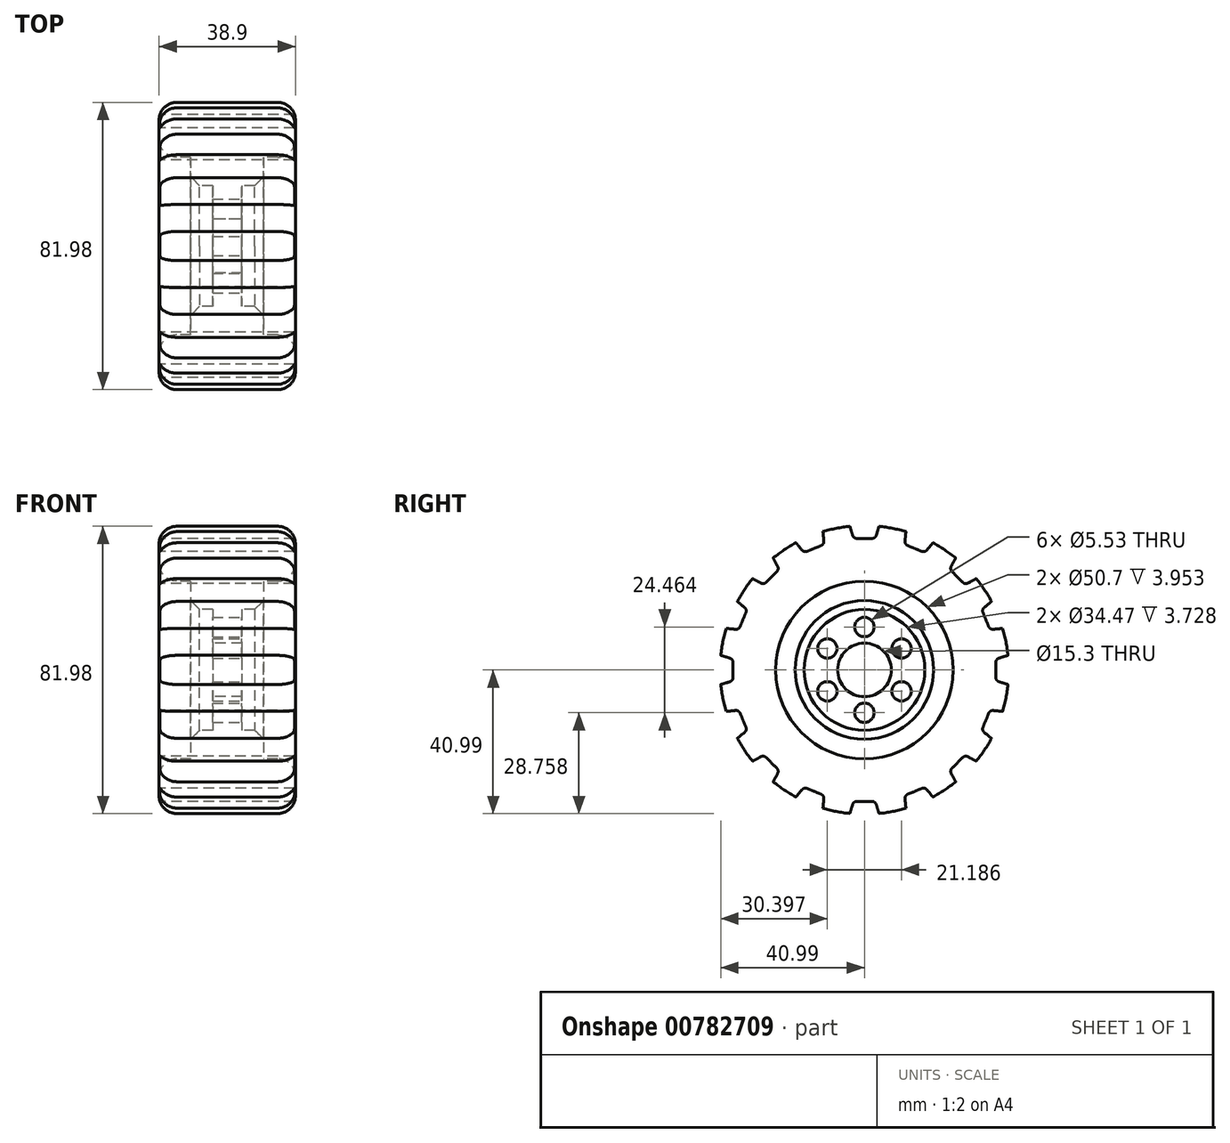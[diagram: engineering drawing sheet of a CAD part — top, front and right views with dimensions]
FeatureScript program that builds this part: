
annotation { "Feature Type Name" : "Feature", "Feature Type Description" : "" }
export const myFeature = defineFeature(function(context is Context, id is Id, definition is map)
    precondition{}
    {
        {
            var Q0;
            Q0=qCreatedBy(makeId("Front.planeOp"),FACE);
            var sketch = newSketch(context, id + "F0", { "sketchPlane" : qUnion([Q0])});
            skLineSegment(sketch, "E0", {"start": v(0, 41.2) * mm, "end": v(-19.45, 41.2) * mm});
            skLineSegment(sketch, "E1", {"start": v(-19.45, 41.2) * mm, "end": v(-19.45, 25.35) * mm});
            skLineSegment(sketch, "E2", {"start": v(-19.45, 25.35) * mm, "end": v(-10.42, 25.35) * mm});
            skLineSegment(sketch, "E3", {"start": v(-10.42, 25.35) * mm, "end": v(-10.42, 17.24) * mm});
            skLineSegment(sketch, "E4", {"start": v(-10.42, 17.24) * mm, "end": v(-4.15, 17.24) * mm});
            skLineSegment(sketch, "E5", {"start": v(-4.15, 17.24) * mm, "end": v(-4.15, 7.65) * mm});
            skLineSegment(sketch, "E6", {"start": v(-4.15, 7.65) * mm, "end": v(0, 7.65) * mm});
            skLineSegment(sketch, "E7.MirrorCS", {"start": v(0, 41.2) * mm, "end": v(19.45, 41.2) * mm});
            skLineSegment(sketch, "E8.MirrorCS", {"start": v(19.45, 41.2) * mm, "end": v(19.45, 25.35) * mm});
            skLineSegment(sketch, "E9.MirrorCS", {"start": v(19.45, 25.35) * mm, "end": v(10.42, 25.35) * mm});
            skLineSegment(sketch, "E10.MirrorCS", {"start": v(10.42, 25.35) * mm, "end": v(10.42, 17.24) * mm});
            skLineSegment(sketch, "E11.MirrorCS", {"start": v(10.42, 17.24) * mm, "end": v(4.15, 17.24) * mm});
            skLineSegment(sketch, "E12.MirrorCS", {"start": v(4.15, 7.65) * mm, "end": v(0, 7.65) * mm});
            skLineSegment(sketch, "E13.MirrorCS", {"start": v(4.15, 17.24) * mm, "end": v(4.15, 7.65) * mm});
            skLineSegment(sketch, "E14", {"start": v(-19.63, 0) * mm, "end": v(22.95, 0) * mm});
            skSolve(sketch);
        }
        {
            var Q0;
            Q0=makeQuery(id+"F0.imprint","IMPRINT",FACE,{"disambiguationData":[TD([[makeQuery(id+"F0.imprint","IMPRINT",EDGE,{"derivedFrom":sQuery(id+"F0.wireOp",EDGE,"E0")}),1.0]])]});
            var Q1;
            Q1=sQuery(id+"F0.wireOp",EDGE,"E14");
            revolve(context, id + "F1", {"surfaceOperationType" : NewSurfaceOperationType.NEW, "entities" : qUnion([Q0]), "axis" : qUnion([Q1]), "revolveType" : RevolveType.FULL});
        }
        {
            var Q0;
            Q0=makeQuery(id+"F1.opRevolve","SWEPT_EDGE",EDGE,{"disambiguationData":[OSD([sQuery(id+"F0.wireOp",EDGE,"E0"),sQuery(id+"F0.wireOp",EDGE,"E1")])]});
            var Q1;
            Q1=makeQuery(id+"F1.opRevolve","SWEPT_EDGE",EDGE,{"disambiguationData":[OSD([sQuery(id+"F0.wireOp",EDGE,"E1"),sQuery(id+"F0.wireOp",EDGE,"E2")])]});
            fillet(context, id + "F2", {"entities" : qUnion([Q0, Q1]), "radius" : 5.08 * mm, "tangentPropagation" : true, "allowEdgeOverflow" : false});
        }
        {
            var Q0;
            Q0=makeQuery(id+"F1.opRevolve","SWEPT_EDGE",EDGE,{"disambiguationData":[OSD([sQuery(id+"F0.wireOp",EDGE,"E7.MirrorCS"),sQuery(id+"F0.wireOp",EDGE,"E8.MirrorCS")])]});
            var Q1;
            Q1=makeQuery(id+"F1.opRevolve","SWEPT_EDGE",EDGE,{"disambiguationData":[OSD([sQuery(id+"F0.wireOp",EDGE,"E8.MirrorCS"),sQuery(id+"F0.wireOp",EDGE,"E9.MirrorCS")])]});
            fillet(context, id + "F3", {"entities" : qUnion([Q0, Q1]), "radius" : 5.08 * mm, "tangentPropagation" : true, "allowEdgeOverflow" : false});
        }
        {
            var Q0;
            Q0=makeQuery(id+"F1.opRevolve","SWEPT_EDGE",EDGE,{"disambiguationData":[OSD([sQuery(id+"F0.wireOp",EDGE,"E3"),sQuery(id+"F0.wireOp",EDGE,"E4")])]});
            chamfer(context, id + "F4", {"entities" : qUnion([Q0]), "width" : 2.54 * mm, "tangentPropagation" : true});
        }
        {
            var Q0;
            Q0=makeQuery(id+"F1.opRevolve","SWEPT_EDGE",EDGE,{"disambiguationData":[OSD([sQuery(id+"F0.wireOp",EDGE,"E10.MirrorCS"),sQuery(id+"F0.wireOp",EDGE,"E11.MirrorCS")])]});
            chamfer(context, id + "F5", {"entities" : qUnion([Q0]), "width" : 2.54 * mm, "tangentPropagation" : true});
        }
        {
            var Q0;
            Q0=qCreatedBy(makeId("Right.planeOp"),FACE);
            var sketch = newSketch(context, id + "F6", { "sketchPlane" : qUnion([Q0])});
            skLineSegment(sketch, "E15", {"start": v(4.44, 41.92) * mm, "end": v(3.38, 38.42) * mm});
            skLineSegment(sketch, "E16", {"start": v(2.16, 37.52) * mm, "end": v(0, 37.52) * mm});
            skLineSegment(sketch, "E17.MirrorCS", {"start": v(-4.44, 41.92) * mm, "end": v(-3.38, 38.42) * mm});
            skLineSegment(sketch, "E18.MirrorCS", {"start": v(-2.16, 37.52) * mm, "end": v(0, 37.52) * mm});
            skLineSegment(sketch, "E19", {"start": v(4.44, 41.92) * mm, "end": v(-4.44, 41.92) * mm});
            skPoint(sketch, "E20.visualSharp", {"position": v(3.1, 37.52) * mm});
            skArc(sketch, "E20.filletArc", {"start": v(2.16, 37.52) * mm, "mid": v(2.92, 37.77) * mm, "end": v(3.38, 38.42) * mm});
            skPoint(sketch, "E21.visualSharp", {"position": v(-3.1, 37.52) * mm});
            skArc(sketch, "E21.filletArc", {"start": v(-3.38, 38.42) * mm, "mid": v(-2.92, 37.77) * mm, "end": v(-2.16, 37.52) * mm});
            skLineSegment(sketch, "E22.1.0", {"start": v(-11.94, 40.43) * mm, "end": v(-20.14, 37.03) * mm});
            skLineSegment(sketch, "E22.1.1", {"start": v(-11.94, 40.43) * mm, "end": v(-11.58, 36.79) * mm});
            skArc(sketch, "E22.1.2", {"start": v(-12.36, 35.5) * mm, "mid": v(-11.76, 36.01) * mm, "end": v(-11.58, 36.79) * mm});
            skLineSegment(sketch, "E22.1.3", {"start": v(-12.36, 35.5) * mm, "end": v(-14.36, 34.66) * mm});
            skLineSegment(sketch, "E22.1.4", {"start": v(-16.36, 33.84) * mm, "end": v(-14.36, 34.66) * mm});
            skArc(sketch, "E22.1.5", {"start": v(-17.82, 34.2) * mm, "mid": v(-17.15, 33.78) * mm, "end": v(-16.36, 33.84) * mm});
            skLineSegment(sketch, "E22.1.6", {"start": v(-20.14, 37.03) * mm, "end": v(-17.82, 34.2) * mm});
            skLineSegment(sketch, "E22.2.0", {"start": v(-26.5, 32.78) * mm, "end": v(-32.78, 26.5) * mm});
            skLineSegment(sketch, "E22.2.1", {"start": v(-26.5, 32.78) * mm, "end": v(-24.78, 29.56) * mm});
            skArc(sketch, "E22.2.2", {"start": v(-25, 28.06) * mm, "mid": v(-24.64, 28.77) * mm, "end": v(-24.78, 29.56) * mm});
            skLineSegment(sketch, "E22.2.3", {"start": v(-25, 28.06) * mm, "end": v(-26.53, 26.53) * mm});
            skLineSegment(sketch, "E22.2.4", {"start": v(-28.06, 25) * mm, "end": v(-26.53, 26.53) * mm});
            skArc(sketch, "E22.2.5", {"start": v(-29.56, 24.78) * mm, "mid": v(-28.77, 24.64) * mm, "end": v(-28.06, 25) * mm});
            skLineSegment(sketch, "E22.2.6", {"start": v(-32.78, 26.5) * mm, "end": v(-29.56, 24.78) * mm});
            skLineSegment(sketch, "E22.3.0", {"start": v(-37.03, 20.14) * mm, "end": v(-40.43, 11.94) * mm});
            skLineSegment(sketch, "E22.3.1", {"start": v(-37.03, 20.14) * mm, "end": v(-34.2, 17.82) * mm});
            skArc(sketch, "E22.3.2", {"start": v(-33.84, 16.36) * mm, "mid": v(-33.78, 17.15) * mm, "end": v(-34.2, 17.82) * mm});
            skLineSegment(sketch, "E22.3.3", {"start": v(-33.84, 16.36) * mm, "end": v(-34.66, 14.36) * mm});
            skLineSegment(sketch, "E22.3.4", {"start": v(-35.5, 12.36) * mm, "end": v(-34.66, 14.36) * mm});
            skArc(sketch, "E22.3.5", {"start": v(-36.79, 11.58) * mm, "mid": v(-36.01, 11.76) * mm, "end": v(-35.5, 12.36) * mm});
            skLineSegment(sketch, "E22.3.6", {"start": v(-40.43, 11.94) * mm, "end": v(-36.79, 11.58) * mm});
            skLineSegment(sketch, "E22.4.0", {"start": v(-41.92, 4.44) * mm, "end": v(-41.92, -4.44) * mm});
            skLineSegment(sketch, "E22.4.1", {"start": v(-41.92, 4.44) * mm, "end": v(-38.42, 3.38) * mm});
            skArc(sketch, "E22.4.2", {"start": v(-37.52, 2.16) * mm, "mid": v(-37.77, 2.92) * mm, "end": v(-38.42, 3.38) * mm});
            skLineSegment(sketch, "E22.4.3", {"start": v(-37.52, 2.16) * mm, "end": v(-37.52, 0) * mm});
            skLineSegment(sketch, "E22.4.4", {"start": v(-37.52, -2.16) * mm, "end": v(-37.52, 0) * mm});
            skArc(sketch, "E22.4.5", {"start": v(-38.42, -3.38) * mm, "mid": v(-37.77, -2.92) * mm, "end": v(-37.52, -2.16) * mm});
            skLineSegment(sketch, "E22.4.6", {"start": v(-41.92, -4.44) * mm, "end": v(-38.42, -3.38) * mm});
            skLineSegment(sketch, "E22.5.0", {"start": v(-40.43, -11.94) * mm, "end": v(-37.03, -20.14) * mm});
            skLineSegment(sketch, "E22.5.1", {"start": v(-40.43, -11.94) * mm, "end": v(-36.79, -11.58) * mm});
            skArc(sketch, "E22.5.2", {"start": v(-35.5, -12.36) * mm, "mid": v(-36.01, -11.76) * mm, "end": v(-36.79, -11.58) * mm});
            skLineSegment(sketch, "E22.5.3", {"start": v(-35.5, -12.36) * mm, "end": v(-34.66, -14.36) * mm});
            skLineSegment(sketch, "E22.5.4", {"start": v(-33.84, -16.36) * mm, "end": v(-34.66, -14.36) * mm});
            skArc(sketch, "E22.5.5", {"start": v(-34.2, -17.82) * mm, "mid": v(-33.78, -17.15) * mm, "end": v(-33.84, -16.36) * mm});
            skLineSegment(sketch, "E22.5.6", {"start": v(-37.03, -20.14) * mm, "end": v(-34.2, -17.82) * mm});
            skLineSegment(sketch, "E22.6.0", {"start": v(-32.78, -26.5) * mm, "end": v(-26.5, -32.78) * mm});
            skLineSegment(sketch, "E22.6.1", {"start": v(-32.78, -26.5) * mm, "end": v(-29.56, -24.78) * mm});
            skArc(sketch, "E22.6.2", {"start": v(-28.06, -25) * mm, "mid": v(-28.77, -24.64) * mm, "end": v(-29.56, -24.78) * mm});
            skLineSegment(sketch, "E22.6.3", {"start": v(-28.06, -25) * mm, "end": v(-26.53, -26.53) * mm});
            skLineSegment(sketch, "E22.6.4", {"start": v(-25, -28.06) * mm, "end": v(-26.53, -26.53) * mm});
            skArc(sketch, "E22.6.5", {"start": v(-24.78, -29.56) * mm, "mid": v(-24.64, -28.77) * mm, "end": v(-25, -28.06) * mm});
            skLineSegment(sketch, "E22.6.6", {"start": v(-26.5, -32.78) * mm, "end": v(-24.78, -29.56) * mm});
            skLineSegment(sketch, "E22.7.0", {"start": v(-20.14, -37.03) * mm, "end": v(-11.94, -40.43) * mm});
            skLineSegment(sketch, "E22.7.1", {"start": v(-20.14, -37.03) * mm, "end": v(-17.82, -34.2) * mm});
            skArc(sketch, "E22.7.2", {"start": v(-16.36, -33.84) * mm, "mid": v(-17.15, -33.78) * mm, "end": v(-17.82, -34.2) * mm});
            skLineSegment(sketch, "E22.7.3", {"start": v(-16.36, -33.84) * mm, "end": v(-14.36, -34.66) * mm});
            skLineSegment(sketch, "E22.7.4", {"start": v(-12.36, -35.5) * mm, "end": v(-14.36, -34.66) * mm});
            skArc(sketch, "E22.7.5", {"start": v(-11.58, -36.79) * mm, "mid": v(-11.76, -36.01) * mm, "end": v(-12.36, -35.5) * mm});
            skLineSegment(sketch, "E22.7.6", {"start": v(-11.94, -40.43) * mm, "end": v(-11.58, -36.79) * mm});
            skLineSegment(sketch, "E22.8.0", {"start": v(-4.44, -41.92) * mm, "end": v(4.44, -41.92) * mm});
            skLineSegment(sketch, "E22.8.1", {"start": v(-4.44, -41.92) * mm, "end": v(-3.38, -38.42) * mm});
            skArc(sketch, "E22.8.2", {"start": v(-2.16, -37.52) * mm, "mid": v(-2.92, -37.77) * mm, "end": v(-3.38, -38.42) * mm});
            skLineSegment(sketch, "E22.8.3", {"start": v(-2.16, -37.52) * mm, "end": v(0, -37.52) * mm});
            skLineSegment(sketch, "E22.8.4", {"start": v(2.16, -37.52) * mm, "end": v(0, -37.52) * mm});
            skArc(sketch, "E22.8.5", {"start": v(3.38, -38.42) * mm, "mid": v(2.92, -37.77) * mm, "end": v(2.16, -37.52) * mm});
            skLineSegment(sketch, "E22.8.6", {"start": v(4.44, -41.92) * mm, "end": v(3.38, -38.42) * mm});
            skLineSegment(sketch, "E22.9.0", {"start": v(11.94, -40.43) * mm, "end": v(20.14, -37.03) * mm});
            skLineSegment(sketch, "E22.9.1", {"start": v(11.94, -40.43) * mm, "end": v(11.58, -36.79) * mm});
            skArc(sketch, "E22.9.2", {"start": v(12.36, -35.5) * mm, "mid": v(11.76, -36.01) * mm, "end": v(11.58, -36.79) * mm});
            skLineSegment(sketch, "E22.9.3", {"start": v(12.36, -35.5) * mm, "end": v(14.36, -34.66) * mm});
            skLineSegment(sketch, "E22.9.4", {"start": v(16.36, -33.84) * mm, "end": v(14.36, -34.66) * mm});
            skArc(sketch, "E22.9.5", {"start": v(17.82, -34.2) * mm, "mid": v(17.15, -33.78) * mm, "end": v(16.36, -33.84) * mm});
            skLineSegment(sketch, "E22.9.6", {"start": v(20.14, -37.03) * mm, "end": v(17.82, -34.2) * mm});
            skLineSegment(sketch, "E22.10.0", {"start": v(26.5, -32.78) * mm, "end": v(32.78, -26.5) * mm});
            skLineSegment(sketch, "E22.10.1", {"start": v(26.5, -32.78) * mm, "end": v(24.78, -29.56) * mm});
            skArc(sketch, "E22.10.2", {"start": v(25, -28.06) * mm, "mid": v(24.64, -28.77) * mm, "end": v(24.78, -29.56) * mm});
            skLineSegment(sketch, "E22.10.3", {"start": v(25, -28.06) * mm, "end": v(26.53, -26.53) * mm});
            skLineSegment(sketch, "E22.10.4", {"start": v(28.06, -25) * mm, "end": v(26.53, -26.53) * mm});
            skArc(sketch, "E22.10.5", {"start": v(29.56, -24.78) * mm, "mid": v(28.77, -24.64) * mm, "end": v(28.06, -25) * mm});
            skLineSegment(sketch, "E22.10.6", {"start": v(32.78, -26.5) * mm, "end": v(29.56, -24.78) * mm});
            skLineSegment(sketch, "E22.11.0", {"start": v(37.03, -20.14) * mm, "end": v(40.43, -11.94) * mm});
            skLineSegment(sketch, "E22.11.1", {"start": v(37.03, -20.14) * mm, "end": v(34.2, -17.82) * mm});
            skArc(sketch, "E22.11.2", {"start": v(33.84, -16.36) * mm, "mid": v(33.78, -17.15) * mm, "end": v(34.2, -17.82) * mm});
            skLineSegment(sketch, "E22.11.3", {"start": v(33.84, -16.36) * mm, "end": v(34.66, -14.36) * mm});
            skLineSegment(sketch, "E22.11.4", {"start": v(35.5, -12.36) * mm, "end": v(34.66, -14.36) * mm});
            skArc(sketch, "E22.11.5", {"start": v(36.79, -11.58) * mm, "mid": v(36.01, -11.76) * mm, "end": v(35.5, -12.36) * mm});
            skLineSegment(sketch, "E22.11.6", {"start": v(40.43, -11.94) * mm, "end": v(36.79, -11.58) * mm});
            skLineSegment(sketch, "E22.12.0", {"start": v(41.92, -4.44) * mm, "end": v(41.92, 4.44) * mm});
            skLineSegment(sketch, "E22.12.1", {"start": v(41.92, -4.44) * mm, "end": v(38.42, -3.38) * mm});
            skArc(sketch, "E22.12.2", {"start": v(37.52, -2.16) * mm, "mid": v(37.77, -2.92) * mm, "end": v(38.42, -3.38) * mm});
            skLineSegment(sketch, "E22.12.3", {"start": v(37.52, -2.16) * mm, "end": v(37.52, 0) * mm});
            skLineSegment(sketch, "E22.12.4", {"start": v(37.52, 2.16) * mm, "end": v(37.52, 0) * mm});
            skArc(sketch, "E22.12.5", {"start": v(38.42, 3.38) * mm, "mid": v(37.77, 2.92) * mm, "end": v(37.52, 2.16) * mm});
            skLineSegment(sketch, "E22.12.6", {"start": v(41.92, 4.44) * mm, "end": v(38.42, 3.38) * mm});
            skLineSegment(sketch, "E22.13.0", {"start": v(40.43, 11.94) * mm, "end": v(37.03, 20.14) * mm});
            skLineSegment(sketch, "E22.13.1", {"start": v(40.43, 11.94) * mm, "end": v(36.79, 11.58) * mm});
            skArc(sketch, "E22.13.2", {"start": v(35.5, 12.36) * mm, "mid": v(36.01, 11.76) * mm, "end": v(36.79, 11.58) * mm});
            skLineSegment(sketch, "E22.13.3", {"start": v(35.5, 12.36) * mm, "end": v(34.66, 14.36) * mm});
            skLineSegment(sketch, "E22.13.4", {"start": v(33.84, 16.36) * mm, "end": v(34.66, 14.36) * mm});
            skArc(sketch, "E22.13.5", {"start": v(34.2, 17.82) * mm, "mid": v(33.78, 17.15) * mm, "end": v(33.84, 16.36) * mm});
            skLineSegment(sketch, "E22.13.6", {"start": v(37.03, 20.14) * mm, "end": v(34.2, 17.82) * mm});
            skLineSegment(sketch, "E22.14.0", {"start": v(32.78, 26.5) * mm, "end": v(26.5, 32.78) * mm});
            skLineSegment(sketch, "E22.14.1", {"start": v(32.78, 26.5) * mm, "end": v(29.56, 24.78) * mm});
            skArc(sketch, "E22.14.2", {"start": v(28.06, 25) * mm, "mid": v(28.77, 24.64) * mm, "end": v(29.56, 24.78) * mm});
            skLineSegment(sketch, "E22.14.3", {"start": v(28.06, 25) * mm, "end": v(26.53, 26.53) * mm});
            skLineSegment(sketch, "E22.14.4", {"start": v(25, 28.06) * mm, "end": v(26.53, 26.53) * mm});
            skArc(sketch, "E22.14.5", {"start": v(24.78, 29.56) * mm, "mid": v(24.64, 28.77) * mm, "end": v(25, 28.06) * mm});
            skLineSegment(sketch, "E22.14.6", {"start": v(26.5, 32.78) * mm, "end": v(24.78, 29.56) * mm});
            skLineSegment(sketch, "E22.15.0", {"start": v(20.14, 37.03) * mm, "end": v(11.94, 40.43) * mm});
            skLineSegment(sketch, "E22.15.1", {"start": v(20.14, 37.03) * mm, "end": v(17.82, 34.2) * mm});
            skArc(sketch, "E22.15.2", {"start": v(16.36, 33.84) * mm, "mid": v(17.15, 33.78) * mm, "end": v(17.82, 34.2) * mm});
            skLineSegment(sketch, "E22.15.3", {"start": v(16.36, 33.84) * mm, "end": v(14.36, 34.66) * mm});
            skLineSegment(sketch, "E22.15.4", {"start": v(12.36, 35.5) * mm, "end": v(14.36, 34.66) * mm});
            skArc(sketch, "E22.15.5", {"start": v(11.58, 36.79) * mm, "mid": v(11.76, 36.01) * mm, "end": v(12.36, 35.5) * mm});
            skLineSegment(sketch, "E22.15.6", {"start": v(11.94, 40.43) * mm, "end": v(11.58, 36.79) * mm});
            skPoint(sketch, "E22.center", {"position": v(0, 0) * mm});
            skSolve(sketch);
        }
        {
            var Q0;
            Q0=makeQuery(id+"F6.imprint","IMPRINT",FACE,{"disambiguationData":[TD([[makeQuery(id+"F6.imprint","IMPRINT",EDGE,{"derivedFrom":sQuery(id+"F6.wireOp",EDGE,"E22.14.0")}),1.0]])]});
            var Q1;
            Q1=makeQuery(id+"F6.imprint","IMPRINT",FACE,{"disambiguationData":[TD([[makeQuery(id+"F6.imprint","IMPRINT",EDGE,{"derivedFrom":sQuery(id+"F6.wireOp",EDGE,"E22.15.0")}),1.0]])]});
            var Q2;
            Q2=makeQuery(id+"F6.imprint","IMPRINT",FACE,{"disambiguationData":[TD([[makeQuery(id+"F6.imprint","IMPRINT",EDGE,{"derivedFrom":sQuery(id+"F6.wireOp",EDGE,"E15")}),-1.0]])]});
            var Q3;
            Q3=makeQuery(id+"F6.imprint","IMPRINT",FACE,{"disambiguationData":[TD([[makeQuery(id+"F6.imprint","IMPRINT",EDGE,{"derivedFrom":sQuery(id+"F6.wireOp",EDGE,"E22.13.0")}),1.0]])]});
            var Q4;
            Q4=makeQuery(id+"F6.imprint","IMPRINT",FACE,{"disambiguationData":[TD([[makeQuery(id+"F6.imprint","IMPRINT",EDGE,{"derivedFrom":sQuery(id+"F6.wireOp",EDGE,"E22.12.0")}),1.0]])]});
            var Q5;
            Q5=makeQuery(id+"F6.imprint","IMPRINT",FACE,{"disambiguationData":[TD([[makeQuery(id+"F6.imprint","IMPRINT",EDGE,{"derivedFrom":sQuery(id+"F6.wireOp",EDGE,"E22.11.0")}),1.0]])]});
            var Q6;
            Q6=makeQuery(id+"F6.imprint","IMPRINT",FACE,{"disambiguationData":[TD([[makeQuery(id+"F6.imprint","IMPRINT",EDGE,{"derivedFrom":sQuery(id+"F6.wireOp",EDGE,"E22.10.0")}),1.0]])]});
            var Q7;
            Q7=makeQuery(id+"F6.imprint","IMPRINT",FACE,{"disambiguationData":[TD([[makeQuery(id+"F6.imprint","IMPRINT",EDGE,{"derivedFrom":sQuery(id+"F6.wireOp",EDGE,"E22.9.0")}),1.0]])]});
            var Q8;
            Q8=makeQuery(id+"F6.imprint","IMPRINT",FACE,{"disambiguationData":[TD([[makeQuery(id+"F6.imprint","IMPRINT",EDGE,{"derivedFrom":sQuery(id+"F6.wireOp",EDGE,"E22.8.0")}),1.0]])]});
            var Q9;
            Q9=makeQuery(id+"F6.imprint","IMPRINT",FACE,{"disambiguationData":[TD([[makeQuery(id+"F6.imprint","IMPRINT",EDGE,{"derivedFrom":sQuery(id+"F6.wireOp",EDGE,"E22.7.0")}),1.0]])]});
            var Q10;
            Q10=makeQuery(id+"F6.imprint","IMPRINT",FACE,{"disambiguationData":[TD([[makeQuery(id+"F6.imprint","IMPRINT",EDGE,{"derivedFrom":sQuery(id+"F6.wireOp",EDGE,"E22.6.0")}),1.0]])]});
            var Q11;
            Q11=makeQuery(id+"F6.imprint","IMPRINT",FACE,{"disambiguationData":[TD([[makeQuery(id+"F6.imprint","IMPRINT",EDGE,{"derivedFrom":sQuery(id+"F6.wireOp",EDGE,"E22.5.0")}),1.0]])]});
            var Q12;
            Q12=makeQuery(id+"F6.imprint","IMPRINT",FACE,{"disambiguationData":[TD([[makeQuery(id+"F6.imprint","IMPRINT",EDGE,{"derivedFrom":sQuery(id+"F6.wireOp",EDGE,"E22.4.0")}),1.0]])]});
            var Q13;
            Q13=makeQuery(id+"F6.imprint","IMPRINT",FACE,{"disambiguationData":[TD([[makeQuery(id+"F6.imprint","IMPRINT",EDGE,{"derivedFrom":sQuery(id+"F6.wireOp",EDGE,"E22.3.0")}),1.0]])]});
            var Q14;
            Q14=makeQuery(id+"F6.imprint","IMPRINT",FACE,{"disambiguationData":[TD([[makeQuery(id+"F6.imprint","IMPRINT",EDGE,{"derivedFrom":sQuery(id+"F6.wireOp",EDGE,"E22.2.0")}),1.0]])]});
            var Q15;
            Q15=makeQuery(id+"F6.imprint","IMPRINT",FACE,{"disambiguationData":[TD([[makeQuery(id+"F6.imprint","IMPRINT",EDGE,{"derivedFrom":sQuery(id+"F6.wireOp",EDGE,"E22.1.0")}),1.0]])]});
            extrude(context, id + "F7", {"entities" : qUnion([Q0, Q1, Q2, Q3, Q4, Q5, Q6, Q7, Q8, Q9, Q10, Q11, Q12, Q13, Q14, Q15]), "operationType" : NewBodyOperationType.REMOVE, "endBound" : BoundingType.SYMMETRIC, "depth" : 50.8 * mm, "offsetDistance" : 25.4 * mm});
        }
        {
            var Q0;
            Q0=makeQuery(id+"F1.opRevolve","SWEPT_FACE",FACE,{"disambiguationData":[OSD([sQuery(id+"F0.wireOp",EDGE,"E13.MirrorCS")])]});
            var sketch = newSketch(context, id + "F8", { "sketchPlane" : qUnion([Q0])});
            skCircle(sketch, "E23", {"center": v(0, 12.23) * mm, "radius": 2.76 * mm});
            skCircle(sketch, "E24.1.0", {"center": v(-10.6, 6.12) * mm, "radius": 2.76 * mm});
            skCircle(sketch, "E24.2.0", {"center": v(-10.6, -6.12) * mm, "radius": 2.76 * mm});
            skCircle(sketch, "E24.3.0", {"center": v(0, -12.23) * mm, "radius": 2.76 * mm});
            skCircle(sketch, "E24.4.0", {"center": v(10.6, -6.12) * mm, "radius": 2.76 * mm});
            skCircle(sketch, "E24.5.0", {"center": v(10.6, 6.12) * mm, "radius": 2.76 * mm});
            skPoint(sketch, "E24.center", {"position": v(0, 0) * mm});
            skSolve(sketch);
        }
        {
            var Q0;
            Q0=makeQuery(id+"F8.imprint","IMPRINT",FACE,{"disambiguationData":[TD([[makeQuery(id+"F8.imprint","IMPRINT",EDGE,{"derivedFrom":sQuery(id+"F8.wireOp",EDGE,"E24.2.0")}),1.0]])]});
            var Q1;
            Q1=makeQuery(id+"F8.imprint","IMPRINT",FACE,{"disambiguationData":[TD([[makeQuery(id+"F8.imprint","IMPRINT",EDGE,{"derivedFrom":sQuery(id+"F8.wireOp",EDGE,"E24.1.0")}),1.0]])]});
            var Q2;
            Q2=makeQuery(id+"F8.imprint","IMPRINT",FACE,{"disambiguationData":[TD([[makeQuery(id+"F8.imprint","IMPRINT",EDGE,{"derivedFrom":sQuery(id+"F8.wireOp",EDGE,"E23")}),1.0]])]});
            var Q3;
            Q3=makeQuery(id+"F8.imprint","IMPRINT",FACE,{"disambiguationData":[TD([[makeQuery(id+"F8.imprint","IMPRINT",EDGE,{"derivedFrom":sQuery(id+"F8.wireOp",EDGE,"E24.5.0")}),1.0]])]});
            var Q4;
            Q4=makeQuery(id+"F8.imprint","IMPRINT",FACE,{"disambiguationData":[TD([[makeQuery(id+"F8.imprint","IMPRINT",EDGE,{"derivedFrom":sQuery(id+"F8.wireOp",EDGE,"E24.4.0")}),1.0]])]});
            var Q5;
            Q5=makeQuery(id+"F8.imprint","IMPRINT",FACE,{"disambiguationData":[TD([[makeQuery(id+"F8.imprint","IMPRINT",EDGE,{"derivedFrom":sQuery(id+"F8.wireOp",EDGE,"E24.3.0")}),1.0]])]});
            extrude(context, id + "F9", {"entities" : qUnion([Q0, Q1, Q2, Q3, Q4, Q5]), "operationType" : NewBodyOperationType.REMOVE, "endBound" : BoundingType.SYMMETRIC, "oppositeDirection" : true, "depth" : 50.8 * mm, "offsetDistance" : 25.4 * mm});
        }
    });
